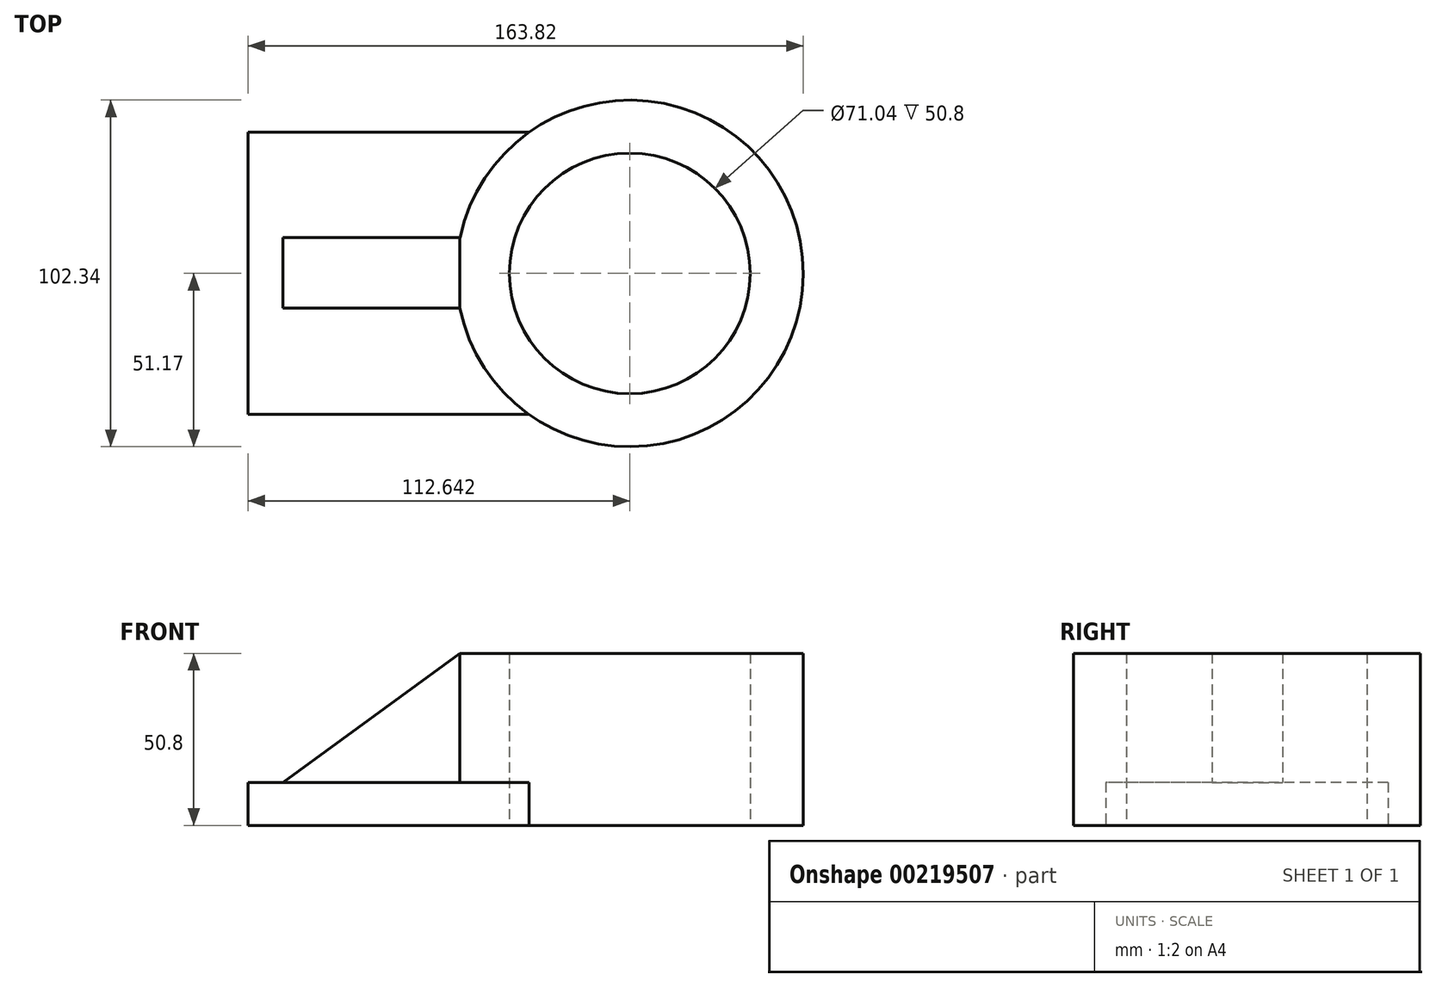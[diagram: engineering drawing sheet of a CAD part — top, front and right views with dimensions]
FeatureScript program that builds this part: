
annotation { "Feature Type Name" : "Feature", "Feature Type Description" : "" }
export const myFeature = defineFeature(function(context is Context, id is Id, definition is map)
    precondition{}
    {
        {
            var Q0;
            Q0=qCreatedBy(makeId("Top.planeOp"),FACE);
            var sketch = newSketch(context, id + "F0", { "sketchPlane" : qUnion([Q0])});
            skCircle(sketch, "E0", {"center": v(63.47, 0) * mm, "radius": 51.17 * mm});
            skCircle(sketch, "E1", {"center": v(63.47, 0) * mm, "radius": 29.7 * mm});
            skLineSegment(sketch, "E2.bottom", {"start": v(33.76, 41.67) * mm, "end": v(-49.17, 41.67) * mm});
            skLineSegment(sketch, "E2.top", {"start": v(33.76, -41.67) * mm, "end": v(-49.17, -41.67) * mm});
            skLineSegment(sketch, "E2.right", {"start": v(-49.17, 41.67) * mm, "end": v(-49.17, -41.67) * mm});
            skPoint(sketch, "E3.start.orphan", {"position": v(33.76, -41.67) * mm});
            skSolve(sketch);
        }
        {
            var Q0;
            Q0 = qSketchRegion(id + "F0", true);
            extrude(context, id + "F1", {"entities" : qUnion([Q0]), "depth" : 12.7 * mm});
        }
        {
            var Q0;
            Q0=makeQuery(id+"F1.opExtrude","CAP_FACE",FACE,{"disambiguationData":[OSD([sQuery(id+"F0.wireOp",EDGE,"E0"),sQuery(id+"F0.wireOp",EDGE,"E1"),sQuery(id+"F0.wireOp",EDGE,"E2.bottom"),sQuery(id+"F0.wireOp",EDGE,"E2.top"),sQuery(id+"F0.wireOp",EDGE,"E2.right")])],"isStart":false});
            var sketch = newSketch(context, id + "F2", { "sketchPlane" : qUnion([Q0])});
            skCircle(sketch, "E4", {"center": v(63.47, 0) * mm, "radius": 51.17 * mm});
            skCircle(sketch, "E5", {"center": v(63.47, 0) * mm, "radius": 35.52 * mm});
            skSolve(sketch);
        }
        {
            var Q0;
            Q0 = qSketchRegion(id + "F2", true);
            extrude(context, id + "F3", {"entities" : qUnion([Q0]), "operationType" : NewBodyOperationType.ADD, "depth" : 38.1 * mm});
        }
        {
            var Q0;
            Q0=makeQuery(id+"F3.opExtrude","CAP_FACE",FACE,{"disambiguationData":[OSD([sQuery(id+"F2.wireOp",EDGE,"E4"),sQuery(id+"F2.wireOp",EDGE,"E5")])],"isStart":false});
            var sketch = newSketch(context, id + "F4", { "sketchPlane" : qUnion([Q0])});
            skCircle(sketch, "E6", {"center": v(63.47, 0) * mm, "radius": 35.52 * mm});
            skSolve(sketch);
        }
        {
            var Q0;
            Q0=makeQuery(id+"F4.imprint","IMPRINT",FACE,{"disambiguationData":[TD([[makeQuery(id+"F4.imprint","IMPRINT",EDGE,{"derivedFrom":sQuery(id+"F4.wireOp",EDGE,"E6")}),1.0]])]});
            extrude(context, id + "F5", {"entities" : qUnion([Q0]), "operationType" : NewBodyOperationType.REMOVE, "oppositeDirection" : true, "depth" : 79.25 * mm});
        }
        {
            var Q0;
            {var subQ0=sQuery(id+"F0.wireOp",EDGE,"E2.right");var subQ1=sQuery(id+"F0.wireOp",EDGE,"E2.top");var subQ2=sQuery(id+"F0.wireOp",EDGE,"E2.bottom");var subQ3=sQuery(id+"F0.wireOp",EDGE,"E0");Q0=makeQuery(id+"F3.boolean.opBoolean","SPLIT",FACE,{"disambiguationData":[TD([makeQuery(id+"F1.opExtrude","SWEPT_FACE",FACE,{"disambiguationData":[OSD([subQ3])]})])],"derivedFrom":makeQuery(id+"F1.opExtrude","CAP_FACE",FACE,{"disambiguationData":[OSD([subQ3,sQuery(id+"F0.wireOp",EDGE,"E1"),subQ2,subQ1,subQ0])],"isStart":false})});}
            var sketch = newSketch(context, id + "F6", { "sketchPlane" : qUnion([Q0])});
            skLineSegment(sketch, "E7.bottom", {"start": v(16.54, -10.28) * mm, "end": v(-38.88, -10.28) * mm});
            skLineSegment(sketch, "E7.top", {"start": v(16.54, 10.58) * mm, "end": v(-38.88, 10.58) * mm});
            skLineSegment(sketch, "E7.left", {"start": v(16.54, -10.28) * mm, "end": v(16.54, 10.58) * mm});
            skLineSegment(sketch, "E7.right", {"start": v(-38.88, -10.28) * mm, "end": v(-38.88, 10.58) * mm});
            skSolve(sketch);
        }
        {
            var Q0;
            Q0 = qSketchRegion(id + "F6", true);
            extrude(context, id + "F7", {"entities" : qUnion([Q0]), "operationType" : NewBodyOperationType.ADD, "depth" : 42.93 * mm});
        }
        {
            var Q0;
            Q0=makeQuery(id+"F7.opExtrude","SWEPT_FACE",FACE,{"disambiguationData":[OSD([sQuery(id+"F6.wireOp",EDGE,"E7.bottom")])]});
            var sketch = newSketch(context, id + "F8", { "sketchPlane" : qUnion([Q0])});
            skLineSegment(sketch, "E8", {"start": v(-38.88, 12.7) * mm, "end": v(13.34, 50.8) * mm});
            skLineSegment(sketch, "E9", {"start": v(13.34, 50.8) * mm, "end": v(16.54, 50.8) * mm});
            skLineSegment(sketch, "E10", {"start": v(16.54, 50.8) * mm, "end": v(16.54, 70.77) * mm});
            skPoint(sketch, "E10.endSnap0", {"position": v(16.54, 53.21) * mm});
            skLineSegment(sketch, "E11", {"start": v(16.54, 70.77) * mm, "end": v(-38.88, 70.77) * mm});
            skLineSegment(sketch, "E12", {"start": v(-38.88, 70.77) * mm, "end": v(-38.88, 12.7) * mm});
            skSolve(sketch);
        }
        {
            var Q0;
            Q0 = qSketchRegion(id + "F8", true);
            extrude(context, id + "F9", {"entities" : qUnion([Q0]), "operationType" : NewBodyOperationType.REMOVE, "oppositeDirection" : true, "depth" : 25.4 * mm});
        }
    });
